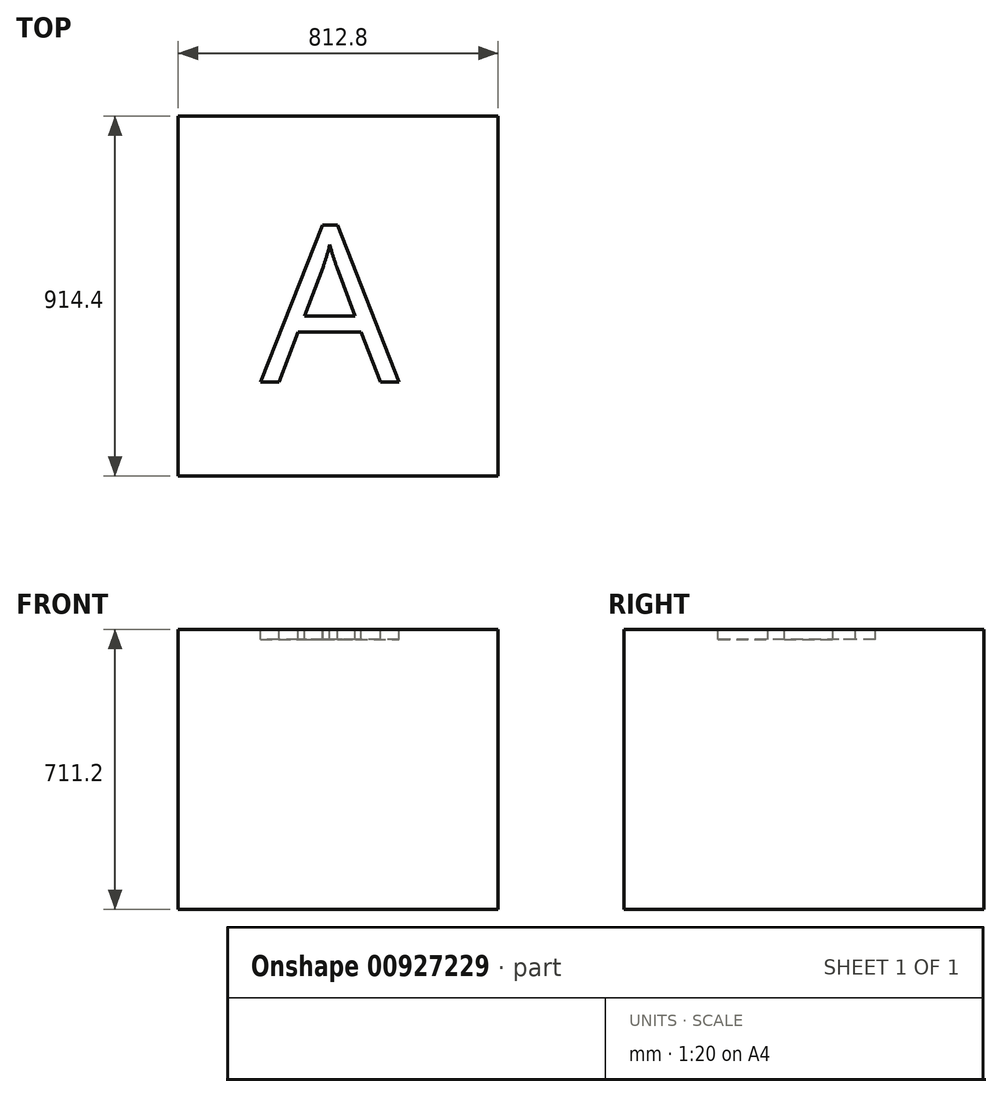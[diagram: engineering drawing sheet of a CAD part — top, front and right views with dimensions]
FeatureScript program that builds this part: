
annotation { "Feature Type Name" : "Feature", "Feature Type Description" : "" }
export const myFeature = defineFeature(function(context is Context, id is Id, definition is map)
    precondition{}
    {
        {
            var Q0;
            Q0=qCreatedBy(makeId("Front.planeOp"),FACE);
            var sketch = newSketch(context, id + "F0", { "sketchPlane" : qUnion([Q0])});
            skLineSegment(sketch, "E0.bottom", {"start": v(406.4, -355.6) * mm, "end": v(-406.4, -355.6) * mm});
            skLineSegment(sketch, "E0.top", {"start": v(406.4, 355.6) * mm, "end": v(-406.4, 355.6) * mm});
            skLineSegment(sketch, "E0.left", {"start": v(406.4, -355.6) * mm, "end": v(406.4, 355.6) * mm});
            skLineSegment(sketch, "E0.right", {"start": v(-406.4, -355.6) * mm, "end": v(-406.4, 355.6) * mm});
            skPoint(sketch, "E0.middle", {"position": v(0, 0) * mm});
            skSolve(sketch);
        }
        {
            var Q0;
            Q0 = qSketchRegion(id + "F0", true);
            extrude(context, id + "F1", {"entities" : qUnion([Q0]), "endBound" : BoundingType.SYMMETRIC, "depth" : 914.4 * mm, "offsetDistance" : 25.4 * mm});
        }
        {
            var Q0;
            Q0=makeQuery(id+"F1.opExtrude","SWEPT_FACE",FACE,{"disambiguationData":[OSD([sQuery(id+"F0.wireOp",EDGE,"E0.top")])]});
            var sketch = newSketch(context, id + "F2", { "sketchPlane" : qUnion([Q0])});
            skText(sketch, "E1", { "text": "A", "fontName": "OpenSans-Regular.ttf"});
            const initialGuessF2  = {"E1": [-0.19742, -0.21825, 1, 0, 0.40093]};
            skSetInitialGuess(sketch, initialGuessF2);
            skSolve(sketch);
        }
        {
            var Q0;
            Q0 = qSketchRegion(id + "F2", true);
            extrude(context, id + "F3", {"entities" : qUnion([Q0]), "operationType" : NewBodyOperationType.REMOVE, "oppositeDirection" : true, "depth" : 25.4 * mm, "offsetDistance" : 25.4 * mm});
        }
    });
